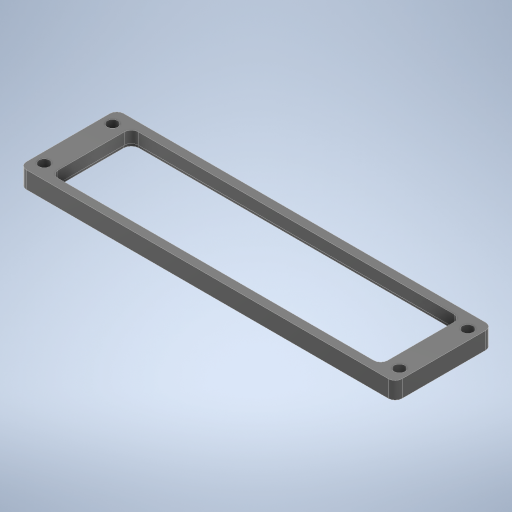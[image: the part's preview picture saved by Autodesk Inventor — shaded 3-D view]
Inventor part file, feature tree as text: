
AUTODESK INVENTOR PART (.ipt)
format: ipt  version: 2024.2 (Build 282272000, 272)  size: 376,320 bytes
history: native  units: mm
features: sketch x2, extrude x2, other x1, hole x1
ambient origin geometry x8: Origin, YZ Plane, XZ Plane, XY Plane, X Axis, Y Axis, Z Axis, Center Point
bodies: Solid1 (feature_tree)
feature tree (6):
  other  "TorsoUpperFrame.ipt"
  sketch  "Sketch2"  dims[d5=0.25mm d6=2.0mm d7=2.25mm d9=2.0mm d10=1.0mm d11=1.0mm d13=5.0mm d14=0.0mm d15=1.6mm d16=0.0mm d19=3.2mm d20=4.0mm d21=4.0mm d22=2.0mm d23=90.0deg d24=8.0mm d25=0.0mm d29=0.0mm d30=0.0mm]
  extrude  "Extrusion1"  Depth=10.0mm
  extrude  "Extrusion2"  Depth=2.0mm
  hole  "Phi3.2"  [1 undecoded]
  sketch  "Sketch1"  dims[d0=10.0mm d4=0.25mm]
note: 1 required parameter value undecoded (feature->parameter linkage not recoverable at this tier; creation-order binding heuristic only, values carry confidence <= 0.55)
